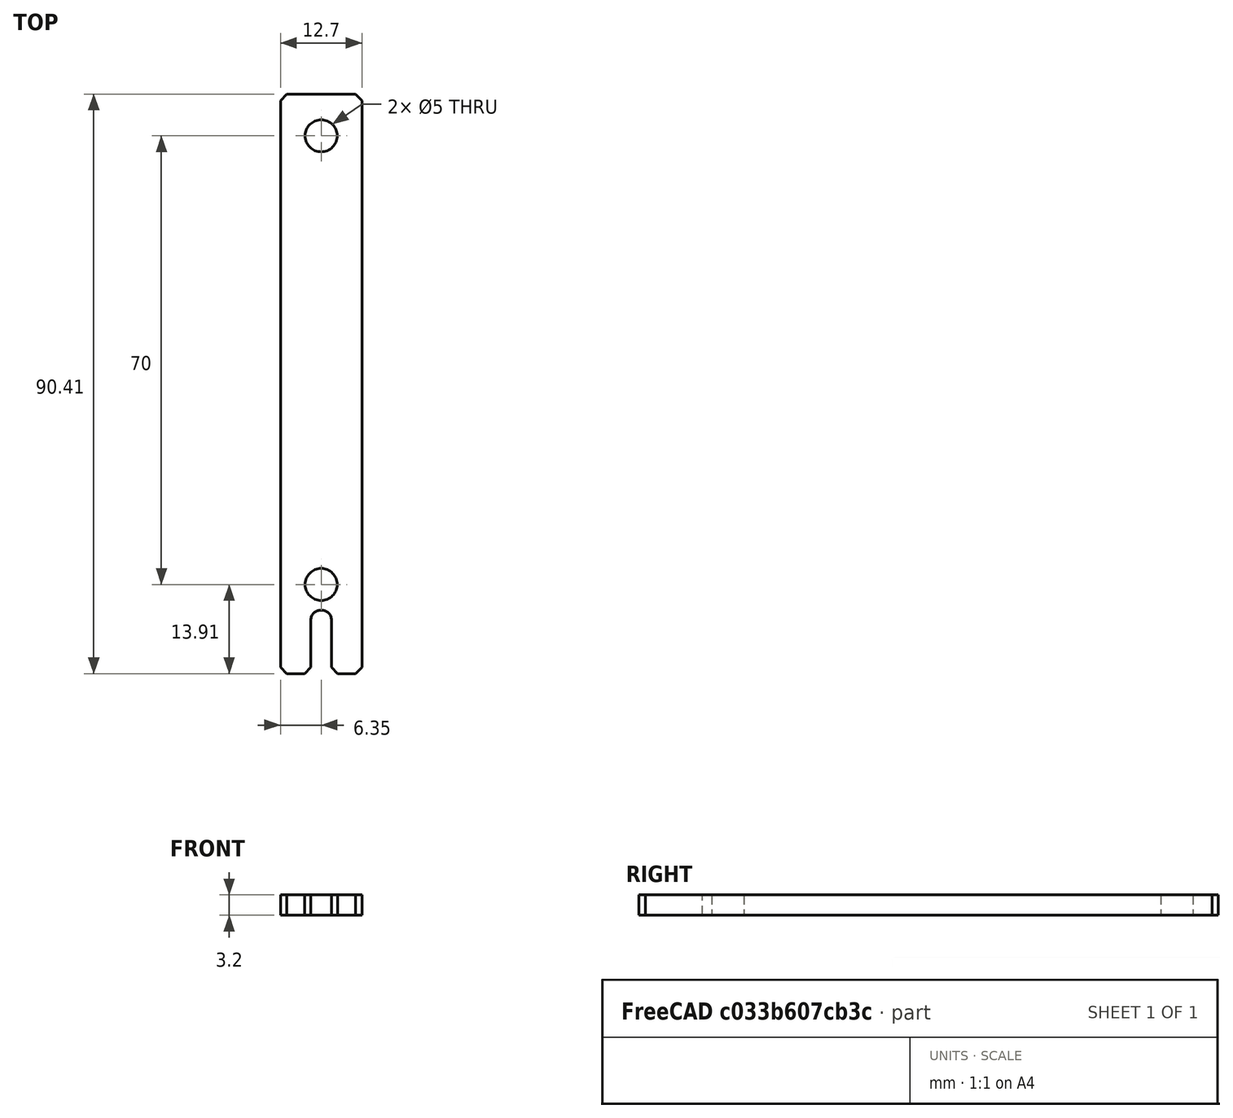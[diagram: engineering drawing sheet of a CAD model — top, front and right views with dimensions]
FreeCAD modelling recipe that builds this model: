
FCSTD DOCUMENT  (FreeCAD 0.16R)
Label: fmjig
License: All rights reserved
LicenseURL: http://en.wikipedia.org/wiki/All_rights_reserved
objects: Sketcher::SketchObject×1, PartDesign::Pad×1, PartDesign::Chamfer×1, Mesh::Feature×1
note: 4 computed .brp shape members not serialized (recipe doc carries the construction recipe); baked Part::Feature solids carry a one-line shape summary decoded from their .brp

FEATURE [Sketcher::SketchObject] Sketch
  sketch-geometry (12):
    g0: LineSegment StartX=-6.35 StartY=100 StartZ=0 EndX=6.35 EndY=100 EndZ=0
    g1: LineSegment StartX=6.35 StartY=100 StartZ=0 EndX=6.35 EndY=9.59173 EndZ=0
    g2: LineSegment StartX=6.35 StartY=9.59173 StartZ=0 EndX=1.6 EndY=9.59173 EndZ=0
    g3: LineSegment StartX=-6.35 StartY=9.59173 StartZ=0 EndX=-6.35 EndY=100 EndZ=0
    g4: Circle CenterX=0 CenterY=93.5 CenterZ=0 NormalX=0 NormalY=0 NormalZ=1 Radius=2.5
    g5: Circle CenterX=0 CenterY=23.5 CenterZ=0 NormalX=0 NormalY=0 NormalZ=1 Radius=2.5
    g6: LineSegment StartX=-0.05 StartY=19.5003 StartZ=0 EndX=0.05 EndY=19.5003 EndZ=0
    g7: LineSegment StartX=1.6 StartY=17.9503 StartZ=0 EndX=1.6 EndY=9.59173 EndZ=0
    g8: LineSegment StartX=-1.6 StartY=17.9503 StartZ=0 EndX=-1.6 EndY=9.59173 EndZ=0
    g9: LineSegment StartX=-1.6 StartY=9.59173 StartZ=0 EndX=-6.35 EndY=9.59173 EndZ=0
    g10: ArcOfCircle CenterX=0.05 CenterY=17.9503 CenterZ=0 NormalX=0 NormalY=0 NormalZ=1 Radius=1.55 StartAngle=0 EndAngle=1.5708
    g11: ArcOfCircle CenterX=-0.05 CenterY=17.9503 CenterZ=0 NormalX=0 NormalY=0 NormalZ=1 Radius=1.55 StartAngle=1.5708 EndAngle=3.14159
  constraints (31):
    c: Coincident(g0,g1)
    c: Coincident(g1,g2)
    c: Coincident(g9,g3)
    c: Coincident(g3,g0)
    c: Horizontal(g0)
    c: Vertical(g1)
    c: Vertical(g3)
    c: Symmetric(g1,g9,g-2)
    c: Distance(g0) = 12.7
    c: Radius(g5) = 2.5
    c: Equal(g5,g4)
    c: PointOnObject(g4,g-2)
    c: PointOnObject(g5,g-2)
    c: DistanceY(g5) = 23.5
    c: DistanceY(g0) = 100
    c: Horizontal(g6)
    c: Vertical(g7)
    c: Vertical(g8)
    c: Coincident(g2,g7)
    c: Coincident(g9,g8)
    c: Tangent(g2,g9)
    c: Distance(g2,g8) = 3.2
    c: Tangent(g7,g10) = 1.5708
    c: Tangent(g6,g10) = 1.5708
    c: Tangent(g8,g11) = -1.5708
    c: Tangent(g6,g11) = 1.5708
    c: Symmetric(g6,g6,g-2)
    c: Symmetric(g2,g8,g-2)
    c: Distance(g6) = 0.1
    c: Distance(g6,g5) = 4
    c: Distance(g2,g5) = 14
FEATURE [PartDesign::Pad] Pad
  Length = 3.2
  Length2 = 100
  Sketch = -> Sketch
  Type = 0
FEATURE [PartDesign::Chamfer] Chamfer
  Base = -> Pad [Edge14,Edge11,Edge17,Edge20,Edge5,Edge8]
  Size = 1
FEATURE [Mesh::Feature] Mesh  label="Chamfer (Meshed)"
